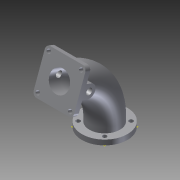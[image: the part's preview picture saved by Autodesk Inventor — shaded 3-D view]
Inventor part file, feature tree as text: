
AUTODESK INVENTOR PART (.ipt)
format: ipt  version: 2011 SP2 (Build 150309200, 309)  size: 260,096 bytes
history: native  units: mm
features: hole x6, sketch x6, extrude x3, fillet x3, sweep x1, plane x1, shell x1, mirror x1, projected_geometry x1
ambient origin geometry x8: Origin, YZ Plane, XZ Plane, XY Plane, X Axis, Y Axis, Z Axis, Center Point
bodies: Solid1 (feature_tree)
feature tree (23):
  sweep  "Sweep1"
  plane  "Work Plane1"
  extrude  "Extrusion1"  Depth=12.217305mm
  extrude  "Extrusion2"  [1 undecoded]
  fillet  "Fillet1"  Radius=45.0mm
  shell  "Shell1"  Thickness=10.0mm
  extrude  "Extrusion3"  Depth=10.0mm TaperAngle=0.0deg
  mirror  "Mirror1"
  fillet  "Fillet2"  Radius=8.0mm
  fillet  "Fillet3"  Radius=10.0mm
  hole  "Hole1"  [1 undecoded]
  hole  "Hole2"  [1 undecoded]
  hole  "Hole3"  [1 undecoded]
  hole  "Hole4"  [1 undecoded]
  hole  "Hole5"  [1 undecoded]
  hole  "Hole6"  [1 undecoded]
  sketch  "Sketch1"  dims[d0=30.0mm d1=25.0mm]
  sketch  "Sketch2"  dims[d2=100.0mm d3=12.217305mm]
  sketch  "Sketch3"  dims[d4=0.0mm d5=-5.0mm d6=45.0mm d7=10.0mm d8=0.0mm]
  sketch  "Sketch4"  dims[d10=80.0mm d11=10.0mm d12=0.0mm d13=8.0mm d14=10.0mm]
  sketch  "Sketch5"  dims[d15=25.0mm d16=22.5mm]
  projected_geometry  "Projected Loop1"
  sketch  "Sketch6"  dims[d17=10.0mm d18=0.0mm d19=10.0mm d20=10.0mm d21=12.0mm d22=6.0mm d23=4.0mm d24=2.0mm d25=90.0deg d26=8.0mm d27=0.0mm d28=10.0mm d29=10.0mm d30=8.0mm d31=6.0mm d32=4.0mm d33=2.0mm d34=90.0deg d35=10.0mm d36=0.0mm d37=10.0mm d38=10.0mm d39=8.0mm d40=6.0mm d41=4.0mm d42=2.0mm d43=90.0deg d44=10.0mm d45=0.0mm d46=10.0mm d47=10.0mm d48=8.0mm d49=6.0mm d50=4.0mm d51=2.0mm d52=90.0deg d53=10.0mm d54=0.0mm d55=10.0mm d56=10.0mm d57=8.0mm d58=6.0mm d59=4.0mm d60=2.0mm d61=90.0deg d62=10.0mm d63=0.0mm d64=37.0mm d65=45.0deg d66=40.0mm d68=360.0deg d70=8.0mm d71=6.0mm d72=4.0mm d73=2.0mm d74=90.0deg d75=10.0mm d76=20.594885mm]
note: 7 required parameter values undecoded (feature->parameter linkage not recoverable at this tier; creation-order binding heuristic only, values carry confidence <= 0.55)
